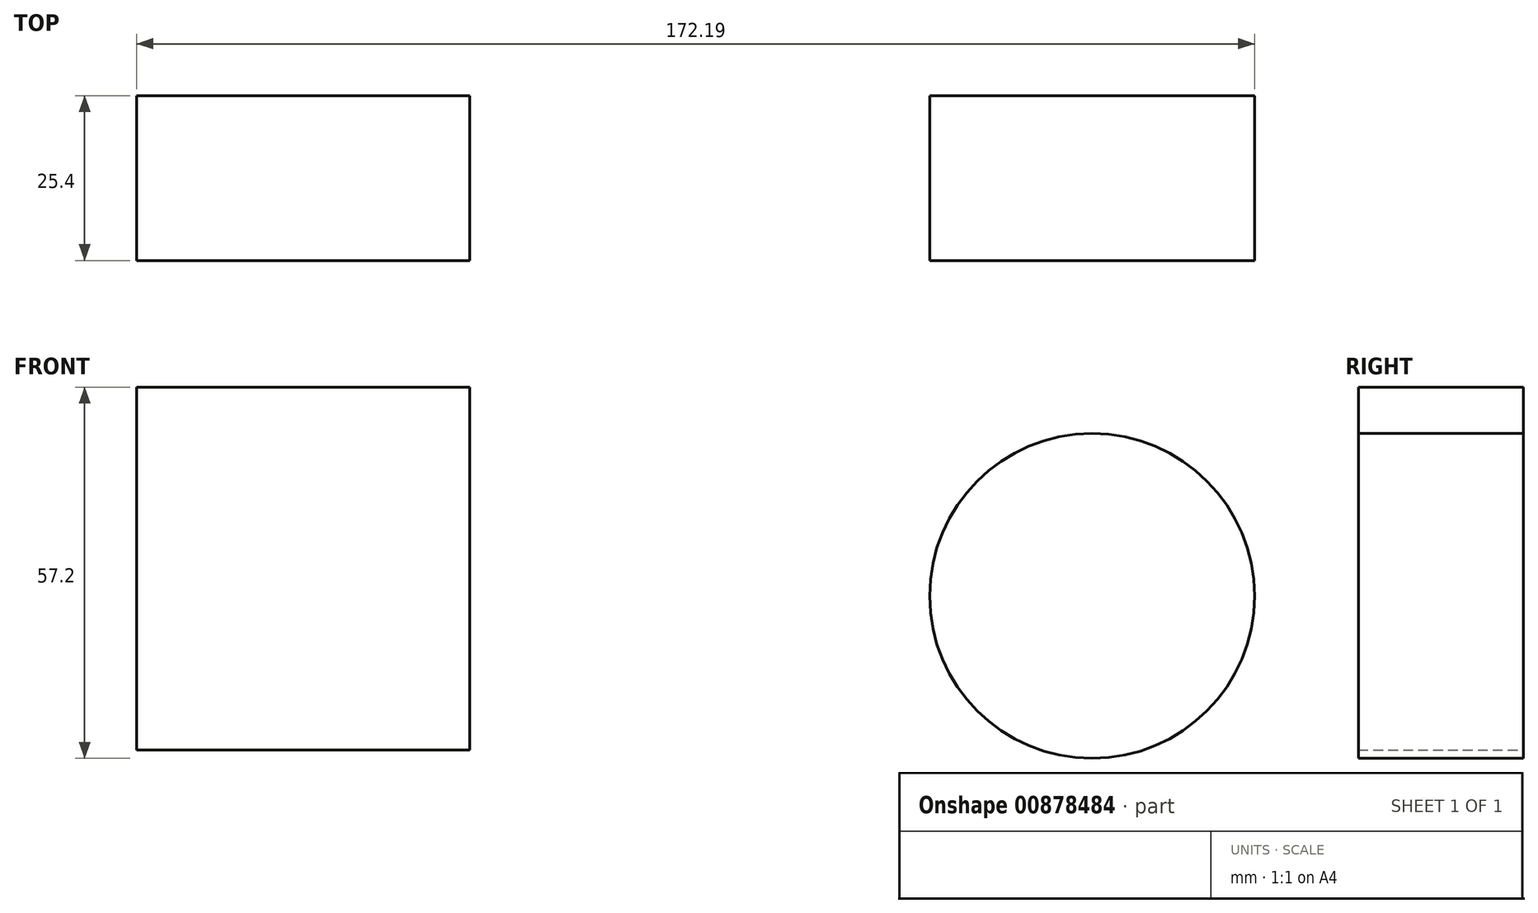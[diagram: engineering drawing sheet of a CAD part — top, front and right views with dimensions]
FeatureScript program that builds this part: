
annotation { "Feature Type Name" : "Feature", "Feature Type Description" : "" }
export const myFeature = defineFeature(function(context is Context, id is Id, definition is map)
    precondition{}
    {
        {
            var Q0;
            Q0=qCreatedBy(makeId("Front.planeOp"),FACE);
            var sketch = newSketch(context, id + "F0", { "sketchPlane" : qUnion([Q0])});
            skLineSegment(sketch, "E0.bottom", {"start": v(-110.81, 32.18) * mm, "end": v(-59.53, 32.18) * mm});
            skLineSegment(sketch, "E0.top", {"start": v(-110.81, -23.7) * mm, "end": v(-59.53, -23.7) * mm});
            skLineSegment(sketch, "E0.left", {"start": v(-110.81, 32.18) * mm, "end": v(-110.81, -23.7) * mm});
            skLineSegment(sketch, "E0.right", {"start": v(-59.53, 32.18) * mm, "end": v(-59.53, -23.7) * mm});
            skCircle(sketch, "E1", {"center": v(36.36, 0) * mm, "radius": 25.02 * mm});
            skSolve(sketch);
        }
        {
            var Q0;
            Q0 = qSketchRegion(id + "F0", true);
            extrude(context, id + "F1", {"entities" : qUnion([Q0]), "depth" : 25.4 * mm, "offsetDistance" : 25.4 * mm});
        }
    });
